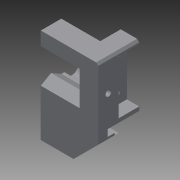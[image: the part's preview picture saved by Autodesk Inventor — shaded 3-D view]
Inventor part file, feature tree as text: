
AUTODESK INVENTOR PART (.ipt)
format: ipt  version: 2015 (Build 190159000, 159)  size: 193,024 bytes
history: native  units: mm
features: extrude x5, hole x5, sketch x5, other x3, chamfer x2
ambient origin geometry x8: Origin, YZ Plane, XZ Plane, XY Plane, X Axis, Y Axis, Z Axis, Center Point
bodies: Body1 (feature_tree)
feature tree (20):
  extrude  "돌출3"  Depth=9.0mm
  extrude  "돌출4"  Depth=30.0mm
  hole  "구멍3"  [1 undecoded]
  hole  "구멍6"  [1 undecoded]
  extrude  "돌출7"  Depth=26.0mm
  other  "두껍게 하기1"
  other  "두껍게 하기2"
  hole  "구멍8"  [1 undecoded]
  extrude  "돌출12"  Depth=5.0mm
  hole  "구멍9"  [1 undecoded]
  extrude  "돌출13"  Depth=0.1mm
  hole  "구멍10"  [1 undecoded]
  other  "두껍게 하기3"
  chamfer  "모따기1"  Distance=0.2mm
  chamfer  "모따기4"  Distance=5.0mm
  sketch  "스케치3"
  sketch  "스케치4"
  sketch  "스케치7"
  sketch  "스케치15"
  sketch  "스케치16"
note: 5 required parameter values undecoded (feature->parameter linkage not recoverable at this tier; creation-order binding heuristic only, values carry confidence <= 0.55)
